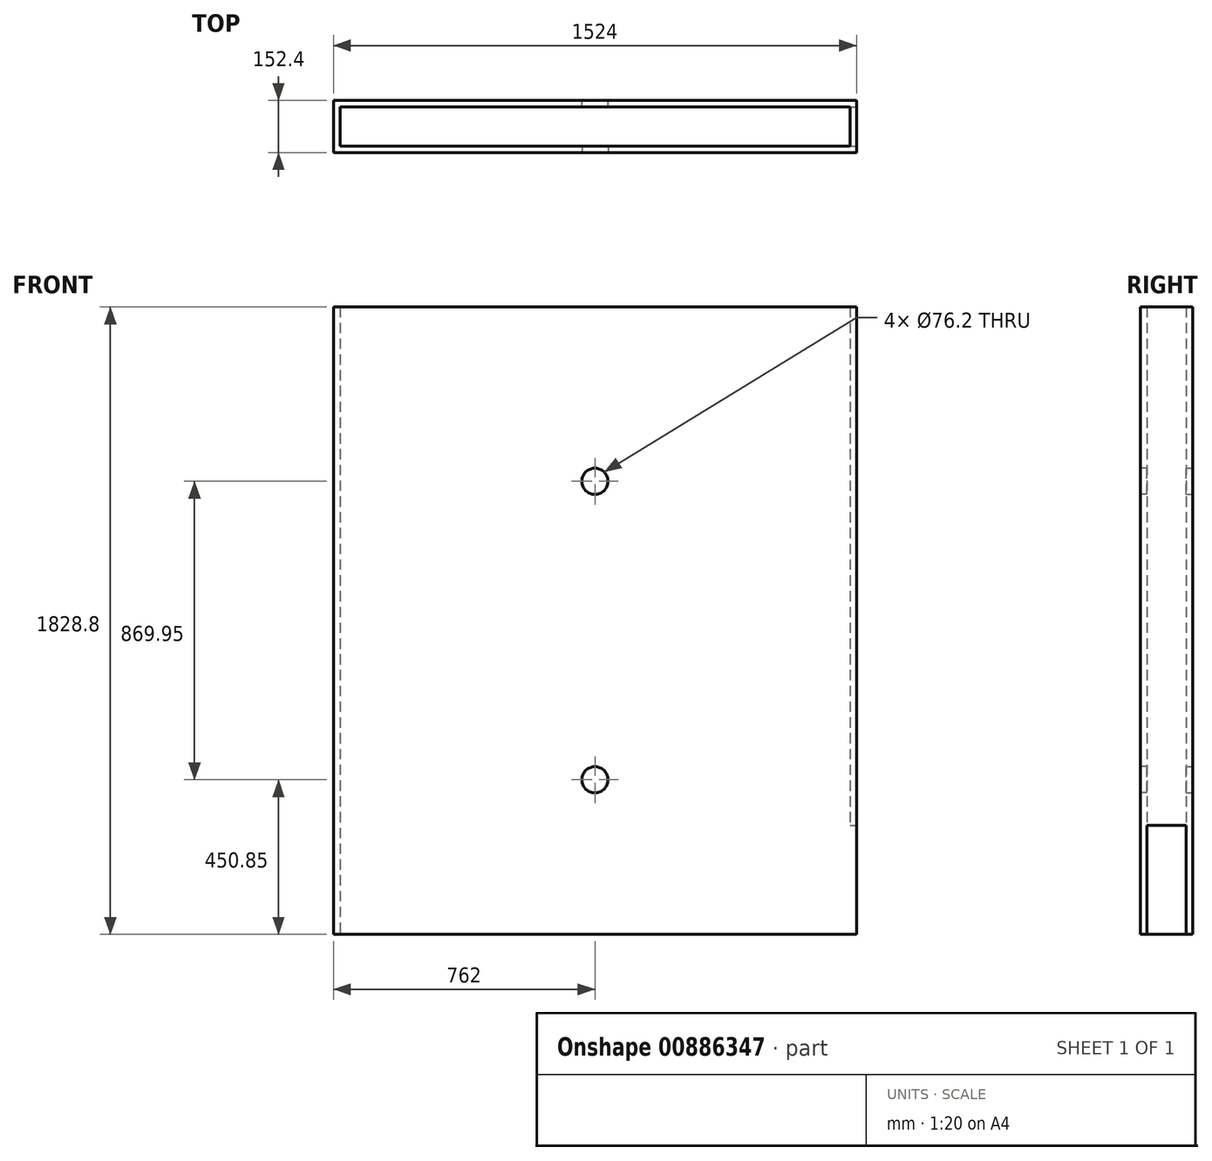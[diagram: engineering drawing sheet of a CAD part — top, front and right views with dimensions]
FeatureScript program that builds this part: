
annotation { "Feature Type Name" : "Feature", "Feature Type Description" : "" }
export const myFeature = defineFeature(function(context is Context, id is Id, definition is map)
    precondition{}
    {
        {
            var Q0;
            Q0=qCreatedBy(makeId("Top.planeOp"),FACE);
            var sketch = newSketch(context, id + "F0", { "sketchPlane" : qUnion([Q0])});
            skLineSegment(sketch, "E0.bottom", {"start": v(762, 76.2) * mm, "end": v(-762, 76.2) * mm});
            skLineSegment(sketch, "E0.top", {"start": v(762, -76.2) * mm, "end": v(-762, -76.2) * mm});
            skLineSegment(sketch, "E0.left", {"start": v(762, 76.2) * mm, "end": v(762, -76.2) * mm});
            skLineSegment(sketch, "E0.right", {"start": v(-762, 76.2) * mm, "end": v(-762, -76.2) * mm});
            skPoint(sketch, "E0.middle", {"position": v(0, 0) * mm});
            skLineSegment(sketch, "E1.bottom", {"start": v(742.95, 57.15) * mm, "end": v(-742.95, 57.15) * mm});
            skLineSegment(sketch, "E1.top", {"start": v(742.95, -57.15) * mm, "end": v(-742.95, -57.15) * mm});
            skLineSegment(sketch, "E1.left", {"start": v(742.95, 57.15) * mm, "end": v(742.95, -57.15) * mm});
            skLineSegment(sketch, "E1.right", {"start": v(-742.95, 57.15) * mm, "end": v(-742.95, -57.15) * mm});
            skSolve(sketch);
        }
        {
            var Q0;
            Q0=makeQuery(id+"F0.imprint","IMPRINT",FACE,{"disambiguationData":[TD([[makeQuery(id+"F0.imprint","IMPRINT",EDGE,{"derivedFrom":sQuery(id+"F0.wireOp",EDGE,"E0.bottom")}),1.0]])]});
            extrude(context, id + "F1", {"entities" : qUnion([Q0]), "depth" : 1828.8 * mm, "offsetDistance" : 25.4 * mm});
        }
        {
            var Q0;
            Q0=makeQuery(id+"F1.opExtrude","SWEPT_FACE",FACE,{"disambiguationData":[OSD([sQuery(id+"F0.wireOp",EDGE,"E0.left")])]});
            var sketch = newSketch(context, id + "F2", { "sketchPlane" : qUnion([Q0])});
            skLineSegment(sketch, "E2", {"start": v(-76.2, 0) * mm, "end": v(-57.15, 0) * mm});
            skLineSegment(sketch, "E3", {"start": v(-57.15, 0) * mm, "end": v(-57.15, 317.5) * mm});
            skLineSegment(sketch, "E4", {"start": v(-57.15, 317.5) * mm, "end": v(57.15, 317.5) * mm});
            skLineSegment(sketch, "E5", {"start": v(57.15, 317.5) * mm, "end": v(57.15, 0) * mm});
            skSolve(sketch);
        }
        {
            var Q0;
            {var subQ0=sQuery(id+"F2.wireOp",EDGE,"E3");Q0=makeQuery(id+"F2.imprint","IMPRINT",FACE,{"disambiguationData":[TD([[makeQuery(id+"F2.imprint","IMPRINT",EDGE,{"derivedFrom":subQ0}),-1.0]])]});}
            extrude(context, id + "F3", {"entities" : qUnion([Q0]), "operationType" : NewBodyOperationType.REMOVE, "oppositeDirection" : true, "depth" : 25.4 * mm, "offsetDistance" : 25.4 * mm});
        }
        {
            var Q0;
            Q0=makeQuery(id+"F1.opExtrude","SWEPT_FACE",FACE,{"disambiguationData":[OSD([sQuery(id+"F0.wireOp",EDGE,"E0.top")])]});
            var sketch = newSketch(context, id + "F4", { "sketchPlane" : qUnion([Q0])});
            skLineSegment(sketch, "E6", {"start": v(0, 1828.8) * mm, "end": v(0, 1320.8) * mm});
            skLineSegment(sketch, "E7", {"start": v(0, 0) * mm, "end": v(0, 450.85) * mm});
            skCircle(sketch, "E8", {"center": v(0, 1320.8) * mm, "radius": 38.1 * mm});
            skCircle(sketch, "E9", {"center": v(0, 450.85) * mm, "radius": 38.1 * mm});
            skSolve(sketch);
        }
        {
            var Q0;
            Q0=makeQuery(id+"F4.imprint","IMPRINT",FACE,{"disambiguationData":[TD([[makeQuery(id+"F4.imprint","IMPRINT",EDGE,{"derivedFrom":sQuery(id+"F4.wireOp",EDGE,"E8")}),1.0]])]});
            var Q1;
            Q1=makeQuery(id+"F4.imprint","IMPRINT",FACE,{"disambiguationData":[TD([[makeQuery(id+"F4.imprint","IMPRINT",EDGE,{"derivedFrom":sQuery(id+"F4.wireOp",EDGE,"E9")}),1.0]])]});
            extrude(context, id + "F5", {"entities" : qUnion([Q0, Q1]), "operationType" : NewBodyOperationType.REMOVE, "oppositeDirection" : true, "depth" : 25.4 * mm, "offsetDistance" : 25.4 * mm});
        }
        {
            var Q0;
            Q0=makeQuery(id+"F1.opExtrude","SWEPT_FACE",FACE,{"disambiguationData":[OSD([sQuery(id+"F0.wireOp",EDGE,"E0.bottom")])]});
            var sketch = newSketch(context, id + "F6", { "sketchPlane" : qUnion([Q0])});
            skLineSegment(sketch, "E10", {"start": v(0, 1828.8) * mm, "end": v(0, 1320.8) * mm});
            skLineSegment(sketch, "E11", {"start": v(0, 0) * mm, "end": v(0, 450.85) * mm});
            skCircle(sketch, "E12", {"center": v(0, 1320.8) * mm, "radius": 38.1 * mm});
            skCircle(sketch, "E13", {"center": v(0, 450.85) * mm, "radius": 38.1 * mm});
            skSolve(sketch);
        }
        {
            var Q0;
            Q0=makeQuery(id+"F6.imprint","IMPRINT",FACE,{"disambiguationData":[TD([[makeQuery(id+"F6.imprint","IMPRINT",EDGE,{"derivedFrom":sQuery(id+"F6.wireOp",EDGE,"E12")}),1.0]])]});
            var Q1;
            Q1=makeQuery(id+"F6.imprint","IMPRINT",FACE,{"disambiguationData":[TD([[makeQuery(id+"F6.imprint","IMPRINT",EDGE,{"derivedFrom":sQuery(id+"F6.wireOp",EDGE,"E13")}),1.0]])]});
            extrude(context, id + "F7", {"entities" : qUnion([Q0, Q1]), "operationType" : NewBodyOperationType.REMOVE, "oppositeDirection" : true, "depth" : 25.4 * mm, "offsetDistance" : 25.4 * mm});
        }
    });
